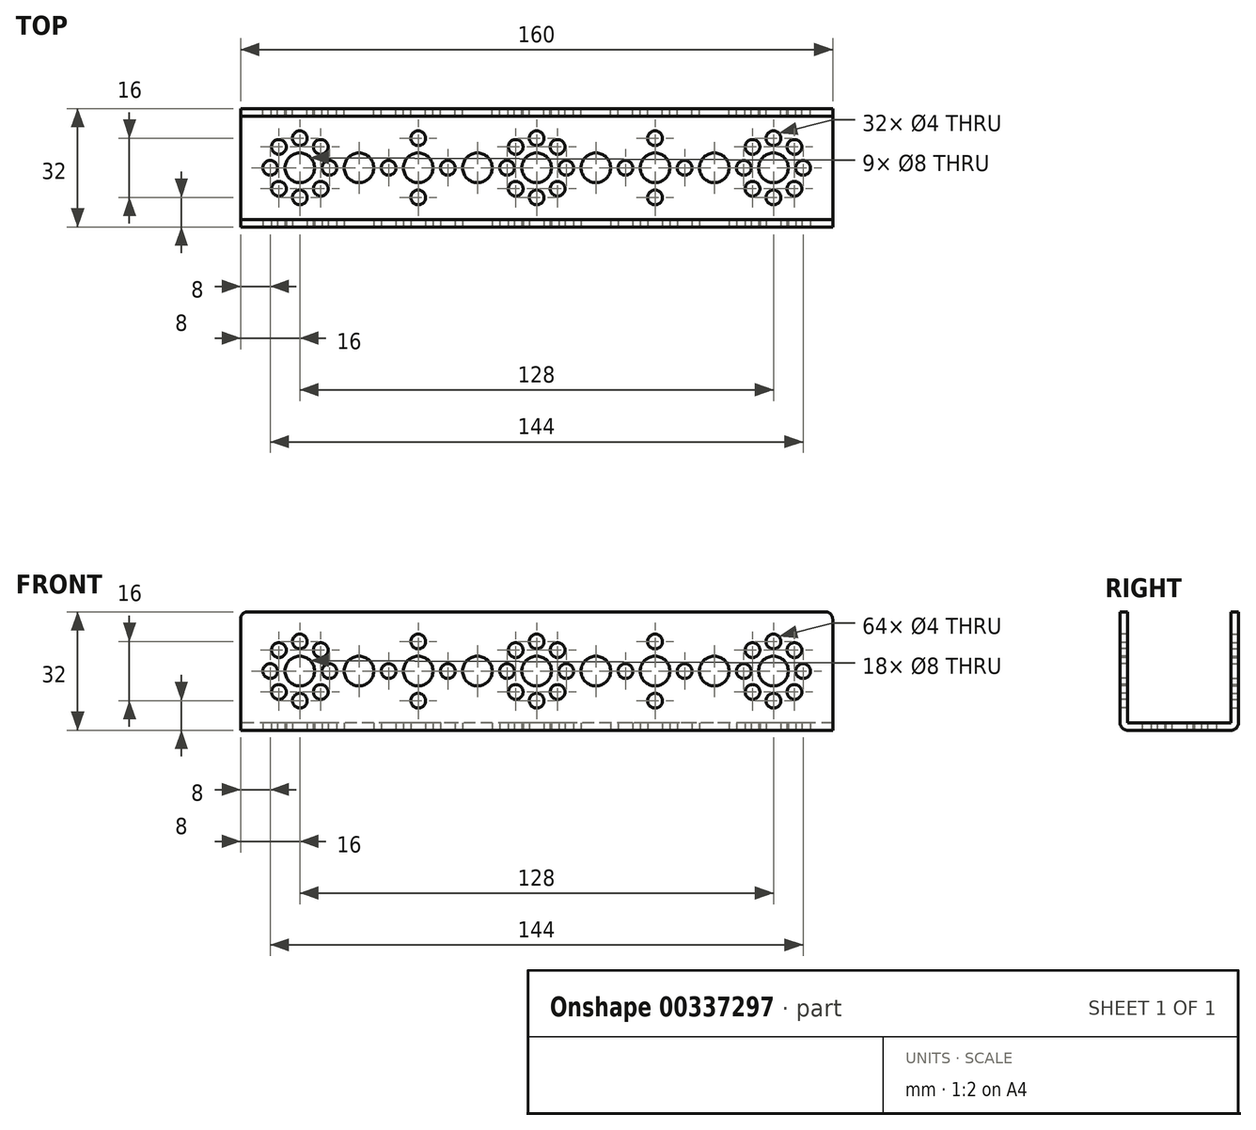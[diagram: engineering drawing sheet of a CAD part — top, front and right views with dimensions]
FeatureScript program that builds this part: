
annotation { "Feature Type Name" : "Feature", "Feature Type Description" : "" }
export const myFeature = defineFeature(function(context is Context, id is Id, definition is map)
    precondition{}
    {
        {
            var Q0;
            Q0=qCreatedBy(makeId("Top.planeOp"),FACE);
            var sketch = newSketch(context, id + "F0", { "sketchPlane" : qUnion([Q0])});
            skLineSegment(sketch, "E0.bottom", {"start": v(80, 16) * mm, "end": v(-80, 16) * mm});
            skLineSegment(sketch, "E0.top", {"start": v(80, -16) * mm, "end": v(-80, -16) * mm});
            skLineSegment(sketch, "E0.left", {"start": v(80, 16) * mm, "end": v(80, -16) * mm});
            skLineSegment(sketch, "E0.right", {"start": v(-80, 16) * mm, "end": v(-80, -16) * mm});
            skPoint(sketch, "E0.middle", {"position": v(0, 0) * mm});
            skLineSegment(sketch, "E1", {"start": v(-64, 2.64) * mm, "end": v(-64, 0) * mm});
            skLineSegment(sketch, "E2", {"start": v(-64, 0) * mm, "end": v(-64, -2.64) * mm});
            skLineSegment(sketch, "E3", {"start": v(-67.98, 0) * mm, "end": v(-64, 0) * mm});
            skLineSegment(sketch, "E4", {"start": v(-62.41, 0) * mm, "end": v(-64, 0) * mm});
            skLineSegment(sketch, "E5", {"start": v(-64, 0) * mm, "end": v(-62.72, 1.28) * mm});
            skLineSegment(sketch, "E6", {"start": v(-64, 0) * mm, "end": v(-65.4, -1.4) * mm});
            skLineSegment(sketch, "E7", {"start": v(-64, 0) * mm, "end": v(-65.4, 1.4) * mm});
            skLineSegment(sketch, "E8", {"start": v(-64, 0) * mm, "end": v(-62.62, -1.38) * mm});
            skCircle(sketch, "E9", {"center": v(-64, 0) * mm, "radius": 4 * mm});
            skCircle(sketch, "E10", {"center": v(-69.66, 5.66) * mm, "radius": 2 * mm});
            skCircle(sketch, "E11", {"center": v(-64, 8) * mm, "radius": 2 * mm});
            skCircle(sketch, "E12", {"center": v(-58.34, 5.66) * mm, "radius": 2 * mm});
            skCircle(sketch, "E13", {"center": v(-56, 0) * mm, "radius": 2 * mm});
            skCircle(sketch, "E14", {"center": v(-72, 0) * mm, "radius": 2 * mm});
            skCircle(sketch, "E15", {"center": v(-69.66, -5.66) * mm, "radius": 2 * mm});
            skCircle(sketch, "E16", {"center": v(-64, -8) * mm, "radius": 2 * mm});
            skCircle(sketch, "E17", {"center": v(-58.34, -5.66) * mm, "radius": 2 * mm});
            skCircle(sketch, "E18", {"center": v(-48, 0) * mm, "radius": 4 * mm});
            skCircle(sketch, "E19", {"center": v(-32, 0) * mm, "radius": 4 * mm});
            skCircle(sketch, "E20", {"center": v(-32, 8) * mm, "radius": 2 * mm});
            skCircle(sketch, "E21", {"center": v(-24, 0) * mm, "radius": 2 * mm});
            skCircle(sketch, "E22", {"center": v(-32, -8) * mm, "radius": 2 * mm});
            skCircle(sketch, "E23", {"center": v(-40, 0) * mm, "radius": 2 * mm});
            skCircle(sketch, "E24", {"center": v(-16, 0) * mm, "radius": 4 * mm});
            skCircle(sketch, "E25.MirrorC", {"center": v(16, 0) * mm, "radius": 4 * mm});
            skCircle(sketch, "E26.MirrorC", {"center": v(24, 0) * mm, "radius": 2 * mm});
            skCircle(sketch, "E27.MirrorC", {"center": v(32, 0) * mm, "radius": 4 * mm});
            skCircle(sketch, "E28.MirrorC", {"center": v(32, 8) * mm, "radius": 2 * mm});
            skCircle(sketch, "E29.MirrorC", {"center": v(40, 0) * mm, "radius": 2 * mm});
            skCircle(sketch, "E30.MirrorC", {"center": v(32, -8) * mm, "radius": 2 * mm});
            skCircle(sketch, "E31.MirrorC", {"center": v(48, 0) * mm, "radius": 4 * mm});
            skCircle(sketch, "E32.MirrorC", {"center": v(64, 8) * mm, "radius": 2 * mm});
            skCircle(sketch, "E33.MirrorC", {"center": v(58.34, 5.66) * mm, "radius": 2 * mm});
            skCircle(sketch, "E34.MirrorC", {"center": v(56, 0) * mm, "radius": 2 * mm});
            skCircle(sketch, "E35.MirrorC", {"center": v(58.34, -5.66) * mm, "radius": 2 * mm});
            skCircle(sketch, "E36.MirrorC", {"center": v(64, -8) * mm, "radius": 2 * mm});
            skCircle(sketch, "E37.MirrorC", {"center": v(69.66, -5.66) * mm, "radius": 2 * mm});
            skCircle(sketch, "E38.MirrorC", {"center": v(72, 0) * mm, "radius": 2 * mm});
            skCircle(sketch, "E39.MirrorC", {"center": v(69.66, 5.66) * mm, "radius": 2 * mm});
            skCircle(sketch, "E40.MirrorC", {"center": v(64, 0) * mm, "radius": 4 * mm});
            skLineSegment(sketch, "E41", {"start": v(0, 2.64) * mm, "end": v(0, 0) * mm});
            skLineSegment(sketch, "E42", {"start": v(0, 0) * mm, "end": v(0, -2.64) * mm});
            skLineSegment(sketch, "E43", {"start": v(-3.98, 0) * mm, "end": v(0, 0) * mm});
            skLineSegment(sketch, "E44", {"start": v(1.59, 0) * mm, "end": v(0, 0) * mm});
            skLineSegment(sketch, "E45", {"start": v(0, 0) * mm, "end": v(1.28, 1.28) * mm});
            skLineSegment(sketch, "E46", {"start": v(0, 0) * mm, "end": v(-1.4, -1.4) * mm});
            skLineSegment(sketch, "E47", {"start": v(0, 0) * mm, "end": v(-1.4, 1.4) * mm});
            skLineSegment(sketch, "E48", {"start": v(0, 0) * mm, "end": v(1.38, -1.38) * mm});
            skCircle(sketch, "E49", {"center": v(0, 0) * mm, "radius": 4 * mm});
            skCircle(sketch, "E50", {"center": v(-5.66, 5.66) * mm, "radius": 2 * mm});
            skCircle(sketch, "E51", {"center": v(0, 8) * mm, "radius": 2 * mm});
            skCircle(sketch, "E52", {"center": v(5.66, 5.66) * mm, "radius": 2 * mm});
            skCircle(sketch, "E53", {"center": v(8, 0) * mm, "radius": 2 * mm});
            skCircle(sketch, "E54", {"center": v(-8, 0) * mm, "radius": 2 * mm});
            skCircle(sketch, "E55", {"center": v(-5.66, -5.66) * mm, "radius": 2 * mm});
            skCircle(sketch, "E56", {"center": v(0, -8) * mm, "radius": 2 * mm});
            skCircle(sketch, "E57", {"center": v(5.66, -5.66) * mm, "radius": 2 * mm});
            skSolve(sketch);
        }
        {
            var Q0;
            Q0=sQuery(id+"F0.wireOp",EDGE,"E0.top");
            var Q1;
            Q1=qCreatedBy(makeId("Front.planeOp"),FACE);
            cPlane(context, id + "F1", {"entities" : qUnion([Q0, Q1]), "cplaneType" : CPlaneType.LINE_ANGLE, "offset" : 25.4 * mm, "angle" : 0 * degree, "width" : 152.4 * mm, "height" : 152.4 * mm});
        }
        {
            var Q0;
            Q0=sQuery(id+"F0.wireOp",EDGE,"E0.bottom");
            var Q1;
            Q1=qCreatedBy(id+"F1.planeOp",FACE);
            cPlane(context, id + "F2", {"entities" : qUnion([Q0, Q1]), "cplaneType" : CPlaneType.LINE_ANGLE, "offset" : 25.4 * mm, "angle" : 0 * degree, "width" : 152.4 * mm, "height" : 152.4 * mm});
        }
        {
            var Q0;
            Q0=qCreatedBy(id+"F2.planeOp",FACE);
            var sketch = newSketch(context, id + "F3", { "sketchPlane" : qUnion([Q0])});
            skLineSegment(sketch, "E58.bottom", {"start": v(80, 0) * mm, "end": v(-80, 0) * mm});
            skLineSegment(sketch, "E58.top", {"start": v(80, 32) * mm, "end": v(-80, 32) * mm});
            skLineSegment(sketch, "E58.left", {"start": v(80, 0) * mm, "end": v(80, 32) * mm});
            skLineSegment(sketch, "E58.right", {"start": v(-80, 0) * mm, "end": v(-80, 32) * mm});
            skLineSegment(sketch, "E59", {"start": v(0, 18.64) * mm, "end": v(0, 16) * mm});
            skLineSegment(sketch, "E60", {"start": v(0, 16) * mm, "end": v(0, 13.36) * mm});
            skLineSegment(sketch, "E61", {"start": v(-3.98, 16) * mm, "end": v(0, 16) * mm});
            skLineSegment(sketch, "E62", {"start": v(1.59, 16) * mm, "end": v(0, 16) * mm});
            skLineSegment(sketch, "E63", {"start": v(0, 16) * mm, "end": v(1.28, 17.28) * mm});
            skLineSegment(sketch, "E64", {"start": v(0, 16) * mm, "end": v(-1.4, 14.6) * mm});
            skLineSegment(sketch, "E65", {"start": v(0, 16) * mm, "end": v(-1.4, 17.4) * mm});
            skLineSegment(sketch, "E66", {"start": v(0, 16) * mm, "end": v(1.38, 14.62) * mm});
            skCircle(sketch, "E67", {"center": v(0, 16) * mm, "radius": 4 * mm});
            skCircle(sketch, "E68", {"center": v(-5.66, 21.66) * mm, "radius": 2 * mm});
            skCircle(sketch, "E69", {"center": v(0, 24) * mm, "radius": 2 * mm});
            skCircle(sketch, "E70", {"center": v(5.66, 21.66) * mm, "radius": 2 * mm});
            skCircle(sketch, "E71", {"center": v(8, 16) * mm, "radius": 2 * mm});
            skCircle(sketch, "E72", {"center": v(-8, 16) * mm, "radius": 2 * mm});
            skCircle(sketch, "E73", {"center": v(-5.66, 10.34) * mm, "radius": 2 * mm});
            skCircle(sketch, "E74", {"center": v(0, 8) * mm, "radius": 2 * mm});
            skCircle(sketch, "E75", {"center": v(5.66, 10.34) * mm, "radius": 2 * mm});
            skPoint(sketch, "E76", {"position": v(80, 16) * mm});
            skLineSegment(sketch, "E77", {"start": v(-64, 18.64) * mm, "end": v(-64, 16) * mm});
            skLineSegment(sketch, "E78", {"start": v(-64, 16) * mm, "end": v(-64, 13.36) * mm});
            skLineSegment(sketch, "E79", {"start": v(-72.14, 16) * mm, "end": v(-64, 16) * mm});
            skLineSegment(sketch, "E80", {"start": v(-64, 16) * mm, "end": v(-66.58, 16) * mm});
            skLineSegment(sketch, "E81", {"start": v(-64, 16) * mm, "end": v(-62.72, 17.28) * mm});
            skLineSegment(sketch, "E82", {"start": v(-64, 16) * mm, "end": v(-65.4, 14.6) * mm});
            skLineSegment(sketch, "E83", {"start": v(-64, 16) * mm, "end": v(-65.4, 17.4) * mm});
            skLineSegment(sketch, "E84", {"start": v(-64, 16) * mm, "end": v(-62.62, 14.62) * mm});
            skCircle(sketch, "E85", {"center": v(-64, 16) * mm, "radius": 4 * mm});
            skCircle(sketch, "E86", {"center": v(-69.66, 21.66) * mm, "radius": 2 * mm});
            skCircle(sketch, "E87", {"center": v(-64, 24) * mm, "radius": 2 * mm});
            skCircle(sketch, "E88", {"center": v(-58.34, 21.66) * mm, "radius": 2 * mm});
            skCircle(sketch, "E89", {"center": v(-56, 16) * mm, "radius": 2 * mm});
            skCircle(sketch, "E90", {"center": v(-72, 16) * mm, "radius": 2 * mm});
            skCircle(sketch, "E91", {"center": v(-69.66, 10.34) * mm, "radius": 2 * mm});
            skCircle(sketch, "E92", {"center": v(-64, 8) * mm, "radius": 2 * mm});
            skCircle(sketch, "E93", {"center": v(-58.34, 10.34) * mm, "radius": 2 * mm});
            skCircle(sketch, "E94", {"center": v(-48, 16) * mm, "radius": 4 * mm});
            skCircle(sketch, "E95", {"center": v(-32, 16) * mm, "radius": 4 * mm});
            skCircle(sketch, "E96", {"center": v(-32, 24) * mm, "radius": 2 * mm});
            skCircle(sketch, "E97", {"center": v(-24, 16) * mm, "radius": 2 * mm});
            skCircle(sketch, "E98", {"center": v(-32, 8) * mm, "radius": 2 * mm});
            skCircle(sketch, "E99", {"center": v(-40, 16) * mm, "radius": 2 * mm});
            skCircle(sketch, "E100", {"center": v(-16, 16) * mm, "radius": 4 * mm});
            skCircle(sketch, "E101.MirrorC", {"center": v(16, 16) * mm, "radius": 4 * mm});
            skCircle(sketch, "E102.MirrorC", {"center": v(24, 16) * mm, "radius": 2 * mm});
            skCircle(sketch, "E103.MirrorC", {"center": v(32, 16) * mm, "radius": 4 * mm});
            skCircle(sketch, "E104.MirrorC", {"center": v(32, 24) * mm, "radius": 2 * mm});
            skCircle(sketch, "E105.MirrorC", {"center": v(32, 8) * mm, "radius": 2 * mm});
            skCircle(sketch, "E106.MirrorC", {"center": v(40, 16) * mm, "radius": 2 * mm});
            skCircle(sketch, "E107.MirrorC", {"center": v(48, 16) * mm, "radius": 4 * mm});
            skCircle(sketch, "E108.MirrorC", {"center": v(56, 16) * mm, "radius": 2 * mm});
            skCircle(sketch, "E109.MirrorC", {"center": v(58.34, 21.66) * mm, "radius": 2 * mm});
            skCircle(sketch, "E110.MirrorC", {"center": v(64, 24) * mm, "radius": 2 * mm});
            skCircle(sketch, "E111.MirrorC", {"center": v(69.66, 21.66) * mm, "radius": 2 * mm});
            skCircle(sketch, "E112.MirrorC", {"center": v(72, 16) * mm, "radius": 2 * mm});
            skCircle(sketch, "E113.MirrorC", {"center": v(69.66, 10.34) * mm, "radius": 2 * mm});
            skCircle(sketch, "E114.MirrorC", {"center": v(64, 8) * mm, "radius": 2 * mm});
            skCircle(sketch, "E115.MirrorC", {"center": v(58.34, 10.34) * mm, "radius": 2 * mm});
            skCircle(sketch, "E116.MirrorC", {"center": v(64, 16) * mm, "radius": 4 * mm});
            skSolve(sketch);
        }
        {
            var Q0;
            Q0=qCreatedBy(id+"F1.planeOp",FACE);
            var sketch = newSketch(context, id + "F4", { "sketchPlane" : qUnion([Q0])});
            skLineSegment(sketch, "E117.bottom", {"start": v(80, 0) * mm, "end": v(-80, 0) * mm});
            skLineSegment(sketch, "E117.top", {"start": v(80, 32) * mm, "end": v(-80, 32) * mm});
            skLineSegment(sketch, "E117.left", {"start": v(80, 0) * mm, "end": v(80, 32) * mm});
            skLineSegment(sketch, "E117.right", {"start": v(-80, 0) * mm, "end": v(-80, 32) * mm});
            skLineSegment(sketch, "E118", {"start": v(-64, 18.64) * mm, "end": v(-64, 16) * mm});
            skLineSegment(sketch, "E119", {"start": v(-64, 16) * mm, "end": v(-64, 13.36) * mm});
            skLineSegment(sketch, "E120", {"start": v(-75.07, 16) * mm, "end": v(-64, 16) * mm});
            skLineSegment(sketch, "E121", {"start": v(-64, 16) * mm, "end": v(-69.5, 16) * mm});
            skLineSegment(sketch, "E122", {"start": v(-64, 16) * mm, "end": v(-62.72, 17.28) * mm});
            skLineSegment(sketch, "E123", {"start": v(-64, 16) * mm, "end": v(-65.4, 14.6) * mm});
            skLineSegment(sketch, "E124", {"start": v(-64, 16) * mm, "end": v(-65.4, 17.4) * mm});
            skLineSegment(sketch, "E125", {"start": v(-64, 16) * mm, "end": v(-62.62, 14.62) * mm});
            skCircle(sketch, "E126", {"center": v(-64, 16) * mm, "radius": 4 * mm});
            skCircle(sketch, "E127", {"center": v(-69.66, 21.66) * mm, "radius": 2 * mm});
            skCircle(sketch, "E128", {"center": v(-64, 24) * mm, "radius": 2 * mm});
            skCircle(sketch, "E129", {"center": v(-58.34, 21.66) * mm, "radius": 2 * mm});
            skCircle(sketch, "E130", {"center": v(-56, 16) * mm, "radius": 2 * mm});
            skCircle(sketch, "E131", {"center": v(-72, 16) * mm, "radius": 2 * mm});
            skCircle(sketch, "E132", {"center": v(-69.66, 10.34) * mm, "radius": 2 * mm});
            skCircle(sketch, "E133", {"center": v(-64, 8) * mm, "radius": 2 * mm});
            skCircle(sketch, "E134", {"center": v(-58.34, 10.34) * mm, "radius": 2 * mm});
            skCircle(sketch, "E135", {"center": v(-48, 16) * mm, "radius": 4 * mm});
            skCircle(sketch, "E136", {"center": v(-32, 16) * mm, "radius": 4 * mm});
            skCircle(sketch, "E137", {"center": v(-32, 24) * mm, "radius": 2 * mm});
            skCircle(sketch, "E138", {"center": v(-24, 16) * mm, "radius": 2 * mm});
            skCircle(sketch, "E139", {"center": v(-32, 8) * mm, "radius": 2 * mm});
            skCircle(sketch, "E140", {"center": v(-40, 16) * mm, "radius": 2 * mm});
            skCircle(sketch, "E141", {"center": v(-16, 16) * mm, "radius": 4 * mm});
            skPoint(sketch, "E142", {"position": v(-80, 16) * mm});
            skLineSegment(sketch, "E143", {"start": v(0, 18.64) * mm, "end": v(0, 16) * mm});
            skLineSegment(sketch, "E144", {"start": v(0, 16) * mm, "end": v(0, 13.36) * mm});
            skLineSegment(sketch, "E145", {"start": v(-11.07, 16) * mm, "end": v(0, 16) * mm});
            skLineSegment(sketch, "E146", {"start": v(0, 16) * mm, "end": v(-5.5, 16) * mm});
            skLineSegment(sketch, "E147", {"start": v(0, 16) * mm, "end": v(1.28, 17.28) * mm});
            skLineSegment(sketch, "E148", {"start": v(0, 16) * mm, "end": v(-1.4, 14.6) * mm});
            skLineSegment(sketch, "E149", {"start": v(0, 16) * mm, "end": v(-1.4, 17.4) * mm});
            skLineSegment(sketch, "E150", {"start": v(0, 16) * mm, "end": v(1.38, 14.62) * mm});
            skCircle(sketch, "E151", {"center": v(0, 16) * mm, "radius": 4 * mm});
            skCircle(sketch, "E152", {"center": v(-5.66, 21.66) * mm, "radius": 2 * mm});
            skCircle(sketch, "E153", {"center": v(0, 24) * mm, "radius": 2 * mm});
            skCircle(sketch, "E154", {"center": v(5.66, 21.66) * mm, "radius": 2 * mm});
            skCircle(sketch, "E155", {"center": v(8, 16) * mm, "radius": 2 * mm});
            skCircle(sketch, "E156", {"center": v(-8, 16) * mm, "radius": 2 * mm});
            skCircle(sketch, "E157", {"center": v(-5.66, 10.34) * mm, "radius": 2 * mm});
            skCircle(sketch, "E158", {"center": v(0, 8) * mm, "radius": 2 * mm});
            skCircle(sketch, "E159", {"center": v(5.66, 10.34) * mm, "radius": 2 * mm});
            skCircle(sketch, "E160.MirrorC", {"center": v(16, 16) * mm, "radius": 4 * mm});
            skCircle(sketch, "E161.MirrorC", {"center": v(24, 16) * mm, "radius": 2 * mm});
            skCircle(sketch, "E162.MirrorC", {"center": v(32, 8) * mm, "radius": 2 * mm});
            skCircle(sketch, "E163.MirrorC", {"center": v(32, 16) * mm, "radius": 4 * mm});
            skCircle(sketch, "E164.MirrorC", {"center": v(40, 16) * mm, "radius": 2 * mm});
            skCircle(sketch, "E165.MirrorC", {"center": v(32, 24) * mm, "radius": 2 * mm});
            skCircle(sketch, "E166.MirrorC", {"center": v(48, 16) * mm, "radius": 4 * mm});
            skCircle(sketch, "E167.MirrorC", {"center": v(56, 16) * mm, "radius": 2 * mm});
            skCircle(sketch, "E168.MirrorC", {"center": v(58.34, 21.66) * mm, "radius": 2 * mm});
            skCircle(sketch, "E169.MirrorC", {"center": v(64, 24) * mm, "radius": 2 * mm});
            skCircle(sketch, "E170.MirrorC", {"center": v(69.66, 21.66) * mm, "radius": 2 * mm});
            skCircle(sketch, "E171.MirrorC", {"center": v(72, 16) * mm, "radius": 2 * mm});
            skCircle(sketch, "E172.MirrorC", {"center": v(69.66, 10.34) * mm, "radius": 2 * mm});
            skCircle(sketch, "E173.MirrorC", {"center": v(64, 8) * mm, "radius": 2 * mm});
            skCircle(sketch, "E174.MirrorC", {"center": v(58.34, 10.34) * mm, "radius": 2 * mm});
            skCircle(sketch, "E175.MirrorC", {"center": v(64, 16) * mm, "radius": 4 * mm});
            skSolve(sketch);
        }
        {
            var Q0;
            Q0=makeQuery(id+"F0.imprint","IMPRINT",FACE,{"disambiguationData":[TD([[makeQuery(id+"F0.imprint","IMPRINT",EDGE,{"derivedFrom":sQuery(id+"F0.wireOp",EDGE,"E0.bottom")}),1.0]])]});
            extrude(context, id + "F5", {"entities" : qUnion([Q0]), "depth" : 2 * mm});
        }
        {
            var Q0;
            Q0=makeQuery(id+"F3.imprint","IMPRINT",FACE,{"disambiguationData":[TD([[makeQuery(id+"F3.imprint","IMPRINT",EDGE,{"derivedFrom":sQuery(id+"F3.wireOp",EDGE,"E58.bottom")}),-1.0]])]});
            extrude(context, id + "F6", {"entities" : qUnion([Q0]), "operationType" : NewBodyOperationType.ADD, "depth" : 2 * mm});
        }
        {
            var Q0;
            Q0=makeQuery(id+"F4.imprint","IMPRINT",FACE,{"disambiguationData":[TD([[makeQuery(id+"F4.imprint","IMPRINT",EDGE,{"derivedFrom":sQuery(id+"F4.wireOp",EDGE,"E117.bottom")}),-1.0]])]});
            extrude(context, id + "F7", {"entities" : qUnion([Q0]), "operationType" : NewBodyOperationType.ADD, "depth" : 2 * mm});
        }
        {
            var Q0;
            Q0=makeQuery(id+"F5.opExtrude","CAP_EDGE",EDGE,{"disambiguationData":[OSD([sQuery(id+"F0.wireOp",EDGE,"E0.top")])],"isStart":true});
            var Q1;
            Q1=makeQuery(id+"F5.opExtrude","CAP_EDGE",EDGE,{"disambiguationData":[OSD([sQuery(id+"F0.wireOp",EDGE,"E0.bottom")])],"isStart":true});
            var Q2;
            Q2=makeQuery(id+"F7.opExtrude","SWEPT_EDGE",EDGE,{"disambiguationData":[OSD([sQuery(id+"F4.wireOp",EDGE,"E117.top"),sQuery(id+"F4.wireOp",EDGE,"E117.right")])]});
            var Q3;
            Q3=makeQuery(id+"F6.opExtrude","SWEPT_EDGE",EDGE,{"disambiguationData":[OSD([sQuery(id+"F3.wireOp",EDGE,"E58.top"),sQuery(id+"F3.wireOp",EDGE,"E58.left")])]});
            var Q4;
            Q4=makeQuery(id+"F7.opExtrude","SWEPT_EDGE",EDGE,{"disambiguationData":[OSD([sQuery(id+"F4.wireOp",EDGE,"E117.top"),sQuery(id+"F4.wireOp",EDGE,"E117.left")])]});
            var Q5;
            Q5=makeQuery(id+"F6.opExtrude","SWEPT_EDGE",EDGE,{"disambiguationData":[OSD([sQuery(id+"F3.wireOp",EDGE,"E58.top"),sQuery(id+"F3.wireOp",EDGE,"E58.right")])]});
            fillet(context, id + "F8", {"entities" : qUnion([Q0, Q1, Q2, Q3, Q4, Q5]), "radius" : 2 * mm, "tangentPropagation" : true, "allowEdgeOverflow" : false});
        }
    });
